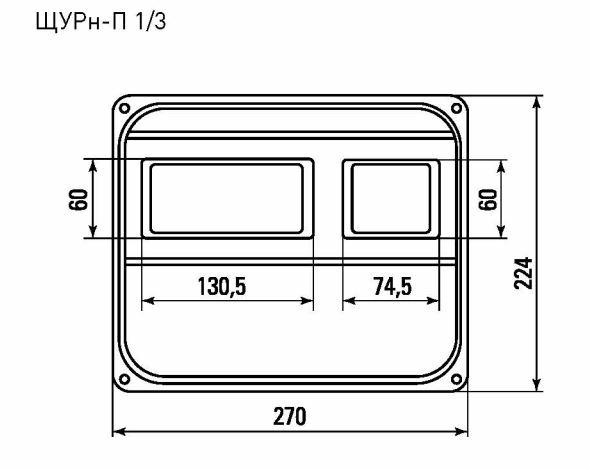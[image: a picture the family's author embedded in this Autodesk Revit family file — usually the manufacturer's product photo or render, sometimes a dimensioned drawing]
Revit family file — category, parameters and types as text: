
# Revit family: EKF_EE_Щит_Этажный_Навесной_ IP31_PROxima
name_source: partatom
category: Электрооборудование
units: mm (PartAtom-declared; Revit-internal decimal feet)

## family parameters
Всегда вертикально = Да
На основе рабочей плоскости = Нет
Общий = Нет
При загрузке вырезать с полостями = Нет
Размер круглого соединителя = Использовать диаметр
Тип детали = Силовой щит
Точка расчета площади = Да

## types (7) — shared parameters
ADSK_Единица измерения = компл.
ADSK_Завод-изготовитель = EKF
ADSK_Количество = 1
ADSK_Материал = RAL 7035_Сталь
ADSK_Размер_Высота = 945 мм
ADSK_Размер_Глубина = 220 мм
ADSK_Размер_Ширина = 880 мм
Изготовитель = EKF
Серия номенклатуры = PROxima
Степень защиты IP = IP31
ТВ = EKF
Тип установки = Навесной
zero-valued in all types: ADSK_Масса, Количество модулей на DIN-рейке

## per-type parameters (varying)
| type | ADSK_Код изделия | ADSK_Марка | ADSK_Наименование | ADSK_Обозначение | Количество DIN-реек | Максимальное количество модулей | Описание | Тип |
| ЩЭ 8 кв. навесной (945х880х220) IP31 EKF PROxima | mb10-n-8 | ЩЭ 8 кв. навесной IP31 | Щит этажный ЩЭ 8 кв. навесной (945х880х220) IP31 EKF PROxima | ЩЭ 8 кв. навесной IP31 | 6 | 36 | Щит этажный ЩЭ 8 кв. навесной (945х880х220) IP31 EKF PROxima | 173 мм |
| ЩЭ 2 кв. навесной (945х880х220) IP31 EKF PROxima | mb10-n-2 | ЩЭ 2 кв. навесной IP31 | Щит этажный ЩЭ 2 кв. навесной (945х880х220) IP31 EKF PROxima | ЩЭ 2 кв. навесной IP31 | 3 | 18 | Щит этажный ЩЭ 2 кв. навесной (945х880х220) IP31 EKF PROxima | 174 мм |
| ЩЭ 3 кв. навесной (945х880х220) IP31 EKF PROxima | mb10-n-3 | ЩЭ 3 кв. навесной IP31 | Щит этажный ЩЭ 3 кв. навесной (945х880х220) IP31 EKF PROxima | ЩЭ 3 кв. навесной IP31 | 6 | 36 | Щит этажный ЩЭ 3 кв. навесной (945х880х220) IP31 EKF PROxima | 175 мм |
| ЩЭ 4 кв. навесной (945х880х220) IP31 EKF PROxima | mb10-n-4 | ЩЭ 4 кв. навесной IP31 | Щит этажный ЩЭ 4 кв. навесной (945х880х220) IP31 EKF PROxima | ЩЭ 4 кв. навесной IP31 | 6 | 36 | Щит этажный ЩЭ 4 кв. навесной (945х880х220) IP31 EKF PROxima | 177 мм |
| ЩЭ 5 кв. навесной (945х880х220) IP31 EKF PROxima | mb10-n-5 | ЩЭ 5 кв. навесной IP31 | Щит этажный ЩЭ 5 кв. навесной (945х880х220) IP31 EKF PROxima | ЩЭ 5 кв. навесной IP31 | 6 | 36 | Щит этажный ЩЭ 5 кв. навесной (945х880х220) IP31 EKF PROxima | 179 мм |
| ЩЭ 6 кв. навесной (945х880х220) IP31 EKF PROxima | mb10-n-6 | ЩЭ 6 кв. навесной IP31 | Щит этажный ЩЭ 6 кв. навесной (945х880х220) IP31 EKF PROxima | ЩЭ 6 кв. навесной IP31 | 6 | 36 | Щит этажный ЩЭ 6 кв. навесной (945х880х220) IP31 EKF PROxima | 180 мм |
| ЩЭ 7 кв. навесной (945х880х220) IP31 EKF PROxima | mb10-n-7 | ЩЭ 7 кв. навесной IP31 | Щит этажный ЩЭ 7 кв. навесной (945х880х220) IP31 EKF PROxima | ЩЭ 7 кв. навесной IP31 | 6 | 36 | Щит этажный ЩЭ 7 кв. навесной (945х880х220) IP31 EKF PROxima | 181 мм |
